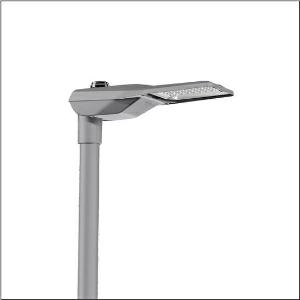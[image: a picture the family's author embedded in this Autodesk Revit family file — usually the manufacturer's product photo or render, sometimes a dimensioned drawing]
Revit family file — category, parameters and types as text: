
# Revit family: streetlight_sl_21_mini___st1_0a_5xe6d37n08gb_0daf
name_source: partatom
category: Lighting Fixtures
units: mm (PartAtom-declared; Revit-internal decimal feet)

## family parameters
Cut with Voids When Loaded = No
Host = Face
Light Source = No
Part Type = Normal
Room Calculation Point = No
Round Connector Dimension = Use Diameter
Shared = No

## types (1)
- --- (1 x LED, 5940 lm, 40.4 W, 3000K)
    Apparent Load = 40 VA
    CIE Flux Codes = 37 72 97 100 100
    Color Rendering = 70
    Color Temperature = 3000K
    Default Elevation = 1800 mm
    Description = Streetlight SL 21 mini, mast luminaire, primary light control with lens, of PMMA, primary optical cover: cover, of toughened safety glass, transparent, light distribution: ST1.0a, light emission: direct distribution, primary light characteristic: asymmetric, installation type: side-entry, LED, 3G 1.5mm², High Power LED, rated luminous flux: 5.940lm, luminous efficacy: 147lm/W, light colour: 730, colour temperature: 3000K, control: overheat protection, pre-setting: linear dimming characteristic, constant luminous flux control, time-dependent luminous flux control, flexible luminous flux parameterisation, mains connection: 230..240V, AC, 50/60Hz, connection cable pre-assembled, cable length: 8,5m, wiring characteristics: H07RN-F, start of lifetime: 40W, end of service life: 41W, reduction: 19W, luminaire housing, of diecast aluminium (EN AC-44300), powder-coated, Siteco® metallic grey (DB 702S), corrosivity category C5 mid according to DIN EN ISO 12944, multi-level sealing system, sealing non-destructively replaceable, inclination adjustable: 0°, 5°, 10°, 15°, length: 628mm, width: 235mm, height: 110mm, spigot size: 42mm (side-entry), protection rating (complete): IP66, insulation class (complete): insulation class I (protective earthing), certification: CE, ENEC, ENEC+, VDE, impact resistance: IK09, permissible operating ambient temperature for outdoor applications: -40..+50°C, standard-compliant lighting for roads and squares, packaging unit: 1 piece

Light Distribution: ST1.0a
    Height = 110 mm
    Lamp = 1 x LED
    Lamp Light Flux = 5940 lm
    Lamp Power = 40.4 W
    Lamp count = 1
    Length = 625 mm
    Luminous efficacy = 147 lm/W
    Manufacturer = Siteco
    ModVariant = No
    Model = 5XE6D37N08GB
    Number of Poles = 1
    OnlyDefault = Yes
    Power Factor = 1
    Product Name = Streetlight SL 21 mini | ST1.0a
    Product group = mast luminaire | pylon top
    ProductGroupID = 6100
    Protection Class = Protection class I
    Protection Degree = IP 66
    RLX_Detail_Level = 1
    RLX_Emergency_Light_Flux = 0 lm
    RLX_Emergency_Type = 0
    RLX_Emergency_Type_DB = No
    RlxData = <blob elided: 91561 chars, md5=bd43501f>
    Socket = socket
    Standby Power = 0 W
    System Light Flux = 5940 lm
    System Power = 40 W
    Type Comments = factory setting: luminous flux: 100 % | dim-lin: 254 | 812 mA
    Type Image = l_1294379.jpg
    URL = http://relux.com
    VarID = @adj_106125
    Voltage = 0 V
    Weight = 0.00 kg
    Width = 234 mm

## geometry (parser evidence)
native form markers: Blend x4, Sweep x10
no freeform markers — native parametric forms only
